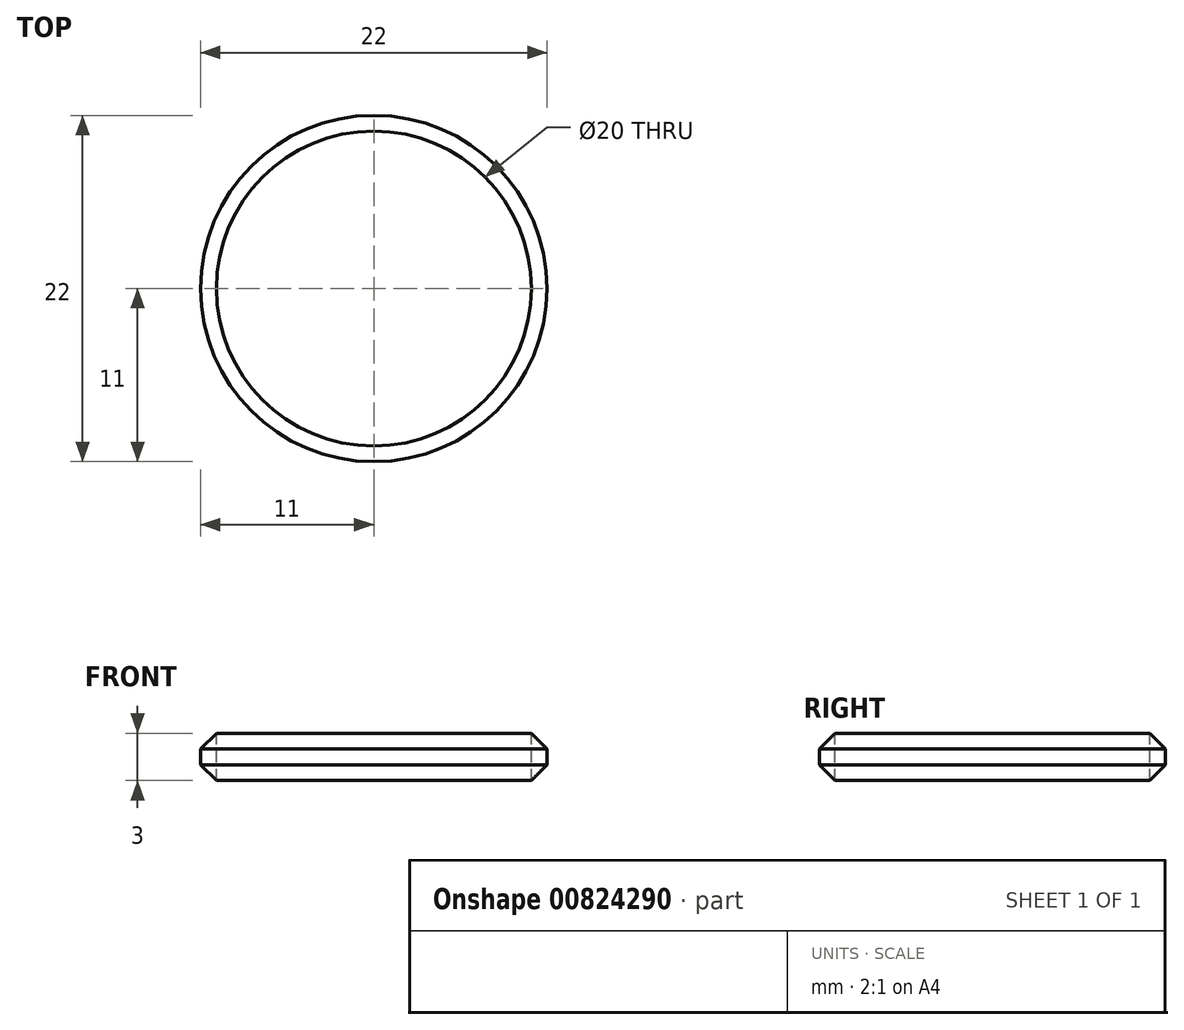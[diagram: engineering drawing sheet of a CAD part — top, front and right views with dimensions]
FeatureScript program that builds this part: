
annotation { "Feature Type Name" : "Feature", "Feature Type Description" : "" }
export const myFeature = defineFeature(function(context is Context, id is Id, definition is map)
    precondition{}
    {
        {
            var Q0;
            Q0=qCreatedBy(makeId("Top.planeOp"),FACE);
            var sketch = newSketch(context, id + "F0", { "sketchPlane" : qUnion([Q0])});
            skCircle(sketch, "E0", {"center": v(0, 0) * mm, "radius": 11 * mm});
            skSolve(sketch);
        }
        {
            var Q0;
            Q0=makeQuery(id+"F0.imprint","IMPRINT",FACE,{"disambiguationData":[TD([[makeQuery(id+"F0.imprint","IMPRINT",EDGE,{"derivedFrom":sQuery(id+"F0.wireOp",EDGE,"E0")}),1.0]])]});
            extrude(context, id + "F1", {"entities" : qUnion([Q0]), "depth" : 3 * mm, "offsetDistance" : 25 * mm});
        }
        {
            var Q0;
            Q0=makeQuery(id+"F1.opExtrude","CAP_FACE",FACE,{"disambiguationData":[OSD([sQuery(id+"F0.wireOp",EDGE,"E0")])],"isStart":false});
            var sketch = newSketch(context, id + "F2", { "sketchPlane" : qUnion([Q0])});
            skCircle(sketch, "E1", {"center": v(0, 0) * mm, "radius": 10 * mm});
            skSolve(sketch);
        }
        {
            var Q0;
            Q0=makeQuery(id+"F2.imprint","IMPRINT",FACE,{"disambiguationData":[TD([[makeQuery(id+"F2.imprint","IMPRINT",EDGE,{"derivedFrom":sQuery(id+"F2.wireOp",EDGE,"E1")}),1.0]])]});
            extrude(context, id + "F3", {"entities" : qUnion([Q0]), "operationType" : NewBodyOperationType.REMOVE, "oppositeDirection" : true, "depth" : 3 * mm, "offsetDistance" : 25 * mm});
        }
        {
            var Q0;
            Q0=makeQuery(id+"F1.opExtrude","CAP_EDGE",EDGE,{"disambiguationData":[OSD([sQuery(id+"F0.wireOp",EDGE,"E0")])],"isStart":false});
            var Q1;
            Q1=makeQuery(id+"F1.opExtrude","CAP_EDGE",EDGE,{"disambiguationData":[OSD([sQuery(id+"F0.wireOp",EDGE,"E0")])],"isStart":true});
            chamfer(context, id + "F4", {"entities" : qUnion([Q0, Q1]), "width" : 1 * mm, "tangentPropagation" : true});
        }
    });
